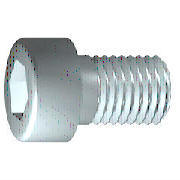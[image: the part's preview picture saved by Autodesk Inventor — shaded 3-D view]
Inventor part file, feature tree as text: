
AUTODESK INVENTOR PART (.ipt)
format: ipt  version: 2022 (Build 260153000, 153)  size: 200,704 bytes
history: native  units: mm (DEFAULTED — no unit token found)
features: sketch x2, other x1, extrude x1, plane x1, fillet x1
ambient origin geometry x7: Origin, YZ Plane, XY Plane, X Axis, Y Axis, Z Axis, Center Point
bodies: Solid1 (feature_tree)
feature tree (6):
  other  "Базовый элемент"
  extrude  "Паз"  Depth=3.9mm
  plane  "Work Plane1"
  fillet  "Fillet2"  Radius=0.429515mm
  sketch  "Эскиз1"
  sketch  "Эскиз2"
